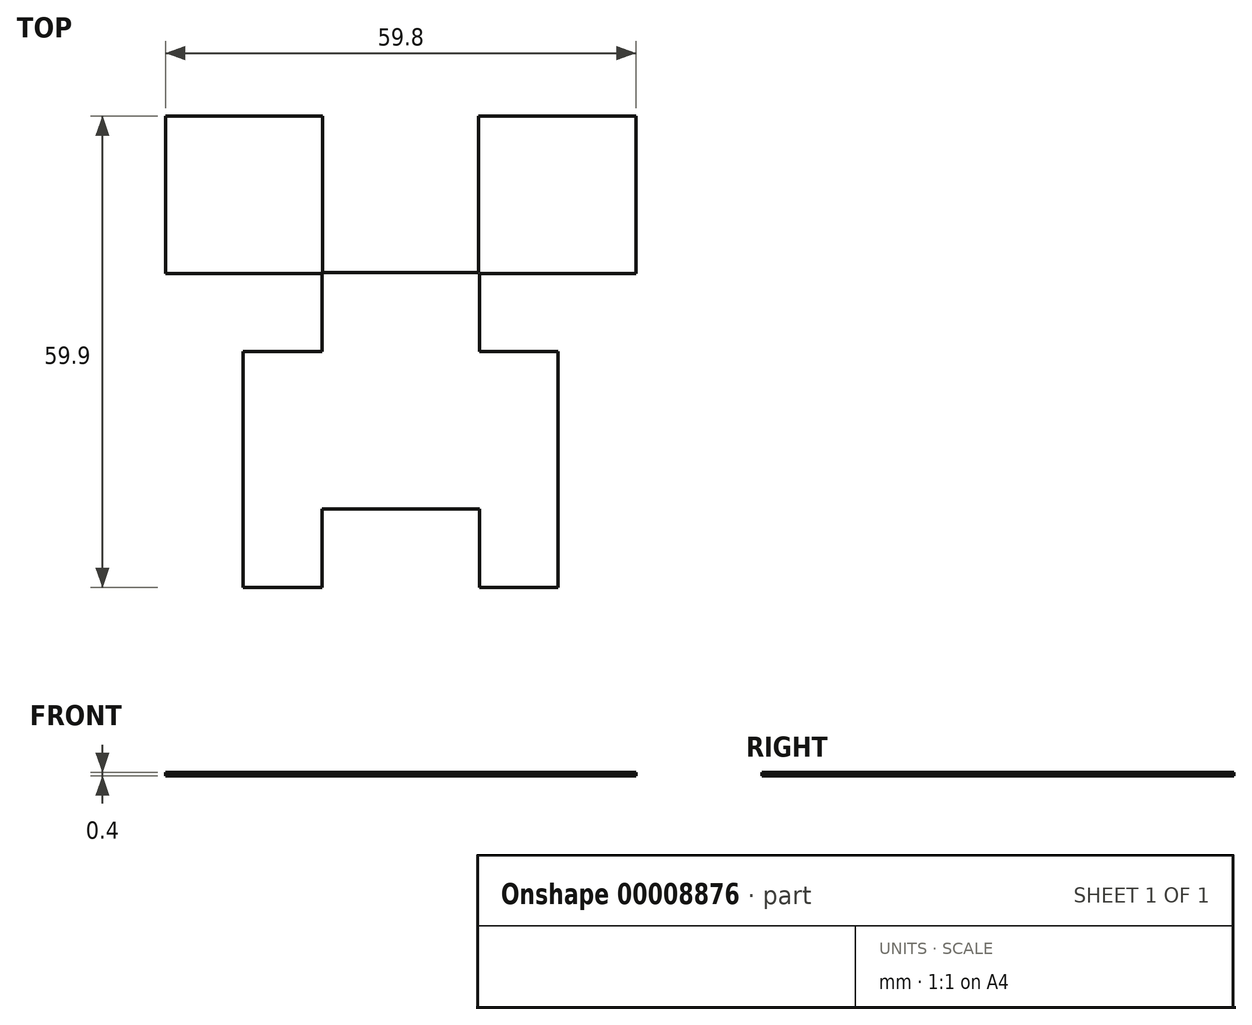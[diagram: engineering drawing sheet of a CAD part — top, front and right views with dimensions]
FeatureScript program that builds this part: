
annotation { "Feature Type Name" : "Feature", "Feature Type Description" : "" }
export const myFeature = defineFeature(function(context is Context, id is Id, definition is map)
    precondition{}
    {
        {
            var Q0;
            Q0=qCreatedBy(makeId("Top.planeOp"),FACE);
            var sketch = newSketch(context, id + "F0", { "sketchPlane" : qUnion([Q0])});
            skLineSegment(sketch, "E0.rect.bottom", {"start": v(10, 5) * mm, "end": v(-10, 5) * mm});
            skLineSegment(sketch, "E0.rect.top", {"start": v(10, -5) * mm, "end": v(-10, -5) * mm});
            skLineSegment(sketch, "E0.rect.left", {"start": v(10, 5) * mm, "end": v(10, -5) * mm});
            skLineSegment(sketch, "E0.rect.right", {"start": v(-10, 5) * mm, "end": v(-10, -5) * mm});
            skPoint(sketch, "E0.rect.middle", {"position": v(0, 0) * mm});
            skSolve(sketch);
        }
        {
            var Q0;
            Q0=makeQuery(id+"F0.imprint","IMPRINT",FACE,{"disambiguationData":[TD([[makeQuery(id+"F0.imprint","IMPRINT",EDGE,{"derivedFrom":sQuery(id+"F0.wireOp",EDGE,"E0.rect.bottom")}),1.0]])]});
            extrude(context, id + "F1", {"entities" : qUnion([Q0]), "depth" : .4 * mm});
        }
        {
            var Q0;
            Q0=qCreatedBy(makeId("Top.planeOp"),FACE);
            var sketch = newSketch(context, id + "F2", { "sketchPlane" : qUnion([Q0])});
            skLineSegment(sketch, "E1.rect.bottom", {"start": v(20, -5) * mm, "end": v(-20, -5) * mm});
            skLineSegment(sketch, "E1.rect.top", {"start": v(20, -25) * mm, "end": v(-20, -25) * mm});
            skLineSegment(sketch, "E1.rect.left", {"start": v(20, -5) * mm, "end": v(20, -25) * mm});
            skLineSegment(sketch, "E1.rect.right", {"start": v(-20, -5) * mm, "end": v(-20, -25) * mm});
            skPoint(sketch, "E1.rect.middle", {"position": v(0, -15) * mm});
            skSolve(sketch);
        }
        {
            var Q0;
            Q0=makeQuery(id+"F2.imprint","IMPRINT",FACE,{"disambiguationData":[TD([[makeQuery(id+"F2.imprint","IMPRINT",EDGE,{"derivedFrom":sQuery(id+"F2.wireOp",EDGE,"E1.rect.bottom")}),1.0]])]});
            var Q1;
            Q1=makeQuery(id+"F1.opExtrude","CAP_FACE",FACE,{"disambiguationData":[OSD([sQuery(id+"F0.wireOp",EDGE,"E0.rect.bottom"),sQuery(id+"F0.wireOp",EDGE,"E0.rect.top"),sQuery(id+"F0.wireOp",EDGE,"E0.rect.left"),sQuery(id+"F0.wireOp",EDGE,"E0.rect.right")])],"isStart":false});
            extrude(context, id + "F3", {"entities" : qUnion([Q0]), "operationType" : NewBodyOperationType.ADD, "endBound" : BoundingType.UP_TO_SURFACE, "endBoundEntityFace" : qUnion([Q1]), "depth" : 0.2 * mm});
        }
        {
            var Q0;
            Q0=qCreatedBy(makeId("Top.planeOp"),FACE);
            var sketch = newSketch(context, id + "F4", { "sketchPlane" : qUnion([Q0])});
            skLineSegment(sketch, "E2.bottom", {"start": v(-20, -25) * mm, "end": v(-10, -25) * mm});
            skLineSegment(sketch, "E2.top", {"start": v(-20, -35) * mm, "end": v(-10, -35) * mm});
            skLineSegment(sketch, "E2.left", {"start": v(-20, -25) * mm, "end": v(-20, -35) * mm});
            skLineSegment(sketch, "E2.right", {"start": v(-10, -25) * mm, "end": v(-10, -35) * mm});
            skLineSegment(sketch, "E3", {"start": v(0, -23.71) * mm, "end": v(0, 0) * mm, "construction": true});
            skLineSegment(sketch, "E4.0.MirrorCS", {"start": v(20, -35) * mm, "end": v(10, -35) * mm});
            skLineSegment(sketch, "E5.0.MirrorCS", {"start": v(10, -25) * mm, "end": v(10, -35) * mm});
            skLineSegment(sketch, "E6.0.MirrorCS", {"start": v(20, -25) * mm, "end": v(20, -35) * mm});
            skLineSegment(sketch, "E7.0.MirrorCS", {"start": v(20, -25) * mm, "end": v(10, -25) * mm});
            skSolve(sketch);
        }
        {
            var Q0;
            Q0=makeQuery(id+"F4.imprint","IMPRINT",FACE,{"disambiguationData":[TD([[makeQuery(id+"F4.imprint","IMPRINT",EDGE,{"derivedFrom":sQuery(id+"F4.wireOp",EDGE,"E2.bottom")}),-1.0]])]});
            var Q1;
            Q1=makeQuery(id+"F4.imprint","IMPRINT",FACE,{"disambiguationData":[TD([[makeQuery(id+"F4.imprint","IMPRINT",EDGE,{"derivedFrom":sQuery(id+"F4.wireOp",EDGE,"E4.0.MirrorCS")}),-1.0]])]});
            var Q2;
            Q2=makeQuery(id+"F3.boolean.opBoolean","MERGE",FACE,{"derivedFrom":[makeQuery(id+"F1.opExtrude","CAP_FACE",FACE,{"disambiguationData":[OSD([sQuery(id+"F0.wireOp",EDGE,"E0.rect.bottom"),sQuery(id+"F0.wireOp",EDGE,"E0.rect.top"),sQuery(id+"F0.wireOp",EDGE,"E0.rect.left"),sQuery(id+"F0.wireOp",EDGE,"E0.rect.right")])],"isStart":false}),makeQuery(id+"F3.opExtrude","CAP_FACE",FACE,{"disambiguationData":[OSD([sQuery(id+"F2.wireOp",EDGE,"E1.rect.bottom"),sQuery(id+"F2.wireOp",EDGE,"E1.rect.top"),sQuery(id+"F2.wireOp",EDGE,"E1.rect.left"),sQuery(id+"F2.wireOp",EDGE,"E1.rect.right")])],"isStart":false})]});
            extrude(context, id + "F5", {"entities" : qUnion([Q0, Q1]), "operationType" : NewBodyOperationType.ADD, "endBound" : BoundingType.UP_TO_SURFACE, "endBoundEntityFace" : qUnion([Q2]), "depth" : 0.2 * mm});
        }
        {
            var Q0;
            Q0=qCreatedBy(makeId("Top.planeOp"),FACE);
            var sketch = newSketch(context, id + "F6", { "sketchPlane" : qUnion([Q0])});
            skLineSegment(sketch, "E8.bottom", {"start": v(-9.9, 4.9) * mm, "end": v(-29.9, 4.9) * mm});
            skLineSegment(sketch, "E8.top", {"start": v(-9.9, 24.9) * mm, "end": v(-29.9, 24.9) * mm});
            skLineSegment(sketch, "E8.left", {"start": v(-9.9, 4.9) * mm, "end": v(-9.9, 24.9) * mm});
            skLineSegment(sketch, "E8.right", {"start": v(-29.9, 4.9) * mm, "end": v(-29.9, 24.9) * mm});
            skLineSegment(sketch, "E9", {"start": v(0, 0) * mm, "end": v(0, 40.48) * mm, "construction": true});
            skLineSegment(sketch, "E10.0.MirrorCS", {"start": v(9.9, 4.9) * mm, "end": v(9.9, 24.9) * mm});
            skLineSegment(sketch, "E11.0.MirrorCS", {"start": v(9.9, 24.9) * mm, "end": v(29.9, 24.9) * mm});
            skLineSegment(sketch, "E12.0.MirrorCS", {"start": v(29.9, 4.9) * mm, "end": v(29.9, 24.9) * mm});
            skLineSegment(sketch, "E13.0.MirrorCS", {"start": v(9.9, 4.9) * mm, "end": v(29.9, 4.9) * mm});
            skSolve(sketch);
        }
        {
            var Q0;
            Q0=makeQuery(id+"F6.imprint","IMPRINT",FACE,{"disambiguationData":[TD([[makeQuery(id+"F6.imprint","IMPRINT",EDGE,{"derivedFrom":sQuery(id+"F6.wireOp",EDGE,"E8.bottom")}),-1.0]])]});
            var Q1;
            Q1=makeQuery(id+"F6.imprint","IMPRINT",FACE,{"disambiguationData":[TD([[makeQuery(id+"F6.imprint","IMPRINT",EDGE,{"derivedFrom":sQuery(id+"F6.wireOp",EDGE,"E10.0.MirrorCS")}),-1.0]])]});
            var Q2;
            Q2=makeQuery(id+"F5.boolean.opBoolean","MERGE",FACE,{"derivedFrom":[makeQuery(id+"F3.boolean.opBoolean","MERGE",FACE,{"derivedFrom":[makeQuery(id+"F1.opExtrude","CAP_FACE",FACE,{"disambiguationData":[OSD([sQuery(id+"F0.wireOp",EDGE,"E0.rect.bottom"),sQuery(id+"F0.wireOp",EDGE,"E0.rect.top"),sQuery(id+"F0.wireOp",EDGE,"E0.rect.left"),sQuery(id+"F0.wireOp",EDGE,"E0.rect.right")])],"isStart":false}),makeQuery(id+"F3.opExtrude","CAP_FACE",FACE,{"disambiguationData":[OSD([sQuery(id+"F2.wireOp",EDGE,"E1.rect.bottom"),sQuery(id+"F2.wireOp",EDGE,"E1.rect.top"),sQuery(id+"F2.wireOp",EDGE,"E1.rect.left"),sQuery(id+"F2.wireOp",EDGE,"E1.rect.right")])],"isStart":false})]}),makeQuery(id+"F5.opExtrude","CAP_FACE",FACE,{"disambiguationData":[OSD([sQuery(id+"F4.wireOp",EDGE,"E2.bottom"),sQuery(id+"F4.wireOp",EDGE,"E2.top"),sQuery(id+"F4.wireOp",EDGE,"E2.left"),sQuery(id+"F4.wireOp",EDGE,"E2.right")])],"isStart":false}),makeQuery(id+"F5.opExtrude","CAP_FACE",FACE,{"disambiguationData":[OSD([sQuery(id+"F4.wireOp",EDGE,"E4.0.MirrorCS"),sQuery(id+"F4.wireOp",EDGE,"E5.0.MirrorCS"),sQuery(id+"F4.wireOp",EDGE,"E6.0.MirrorCS"),sQuery(id+"F4.wireOp",EDGE,"E7.0.MirrorCS")])],"isStart":false})]});
            extrude(context, id + "F7", {"entities" : qUnion([Q0, Q1]), "operationType" : NewBodyOperationType.ADD, "endBound" : BoundingType.UP_TO_SURFACE, "endBoundEntityFace" : qUnion([Q2]), "depth" : 0.2 * mm});
        }
    });
